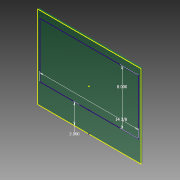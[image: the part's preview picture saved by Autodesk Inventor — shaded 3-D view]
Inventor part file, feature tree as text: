
AUTODESK INVENTOR PART (.ipt)
format: ipt  version: 2015 (Build 190159000, 159)  size: 85,504 bytes
history: native  units: in
note: dims shown in document units (in); Inventor stores cm internally (conversion verified against a paired STEP export)
features: other x4, sketch x2, extrude x1, projected_geometry x1
ambient origin geometry x8: Origin, YZ Plane, XZ Plane, XY Plane, X Axis, Y Axis, Z Axis, Center Point
bodies: Solid1 (feature_tree)
feature tree (8):
  extrude  "Extrusion1"  Depth=15.0in
  sketch  "Sketch2"  dims[d2=0.25in d3=0.0in d4=3.0in d5=14.375in d6=8.0in]
  other  "Work Axis1"
  other  "Work Axis2"
  other  "Work Axis3"
  other  "Work Axis4"
  sketch  "Sketch1"  dims[d0=12.0in d1=15.0in]
  projected_geometry  "Projected Loop1"
